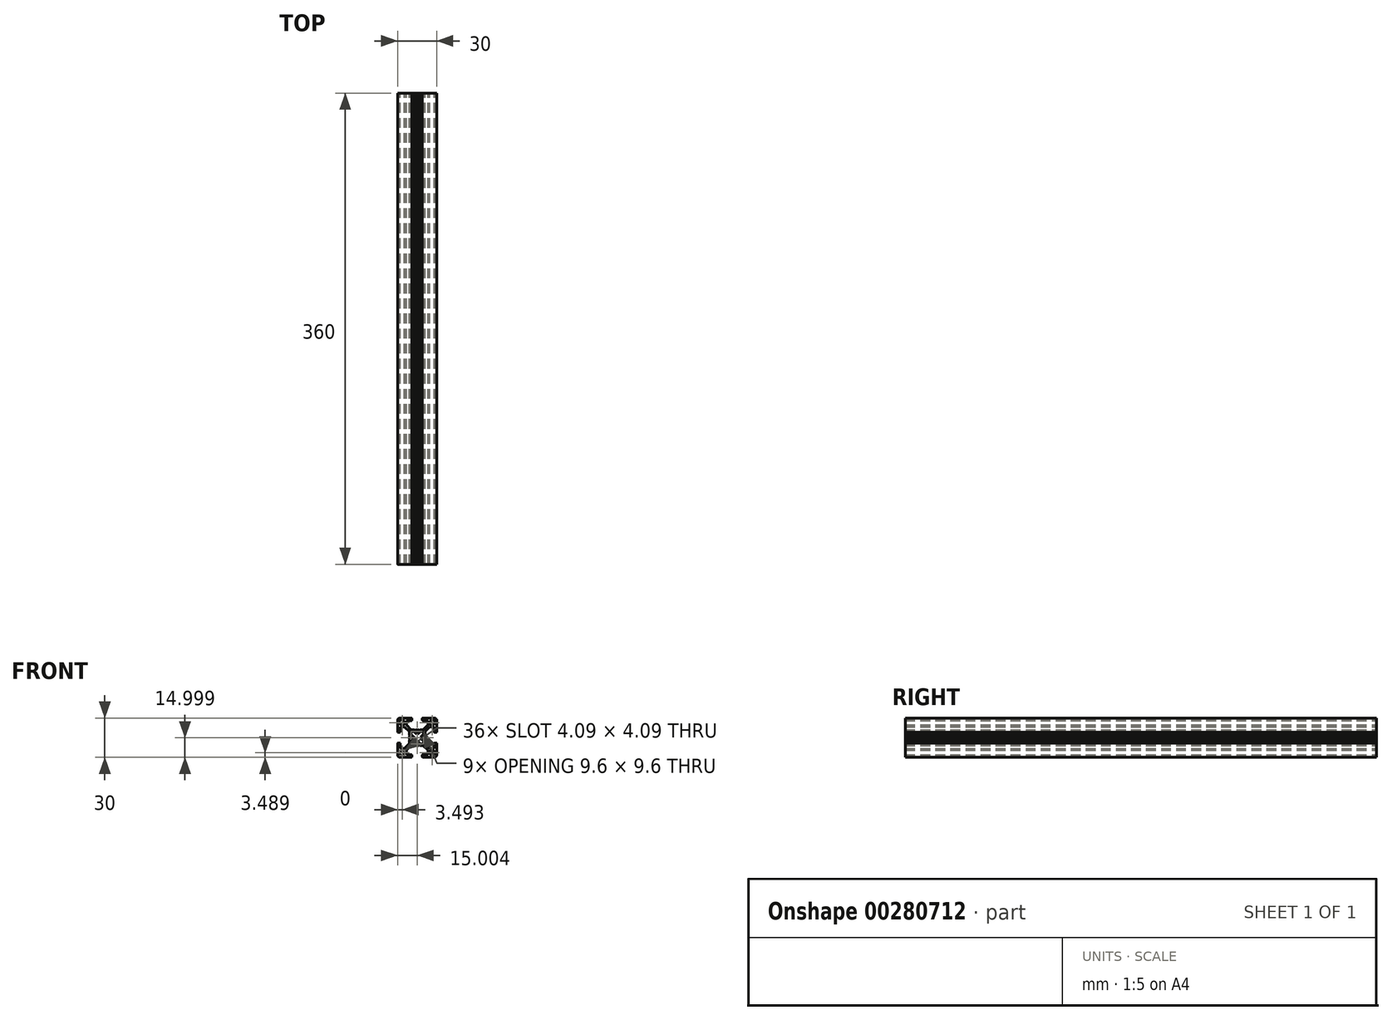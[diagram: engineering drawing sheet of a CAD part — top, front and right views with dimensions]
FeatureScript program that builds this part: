
annotation { "Feature Type Name" : "Feature", "Feature Type Description" : "" }
export const myFeature = defineFeature(function(context is Context, id is Id, definition is map)
    precondition{}
    {
        {
            var Q0;
            Q0=qCreatedBy(makeId("Front.planeOp"),FACE);
            var sketch = newSketch(context, id + "F0", { "sketchPlane" : qUnion([Q0])});
            skArc(sketch, "E0", {"start": v(22.08, 23.36) * mm, "mid": v(21.8, 23.24) * mm, "end": v(21.68, 22.96) * mm});
            skArc(sketch, "E1", {"start": v(21.68, 14.16) * mm, "mid": v(21.8, 13.88) * mm, "end": v(22.08, 13.76) * mm});
            skArc(sketch, "E2", {"start": v(11.48, 5.56) * mm, "mid": v(12.07, 4.15) * mm, "end": v(13.48, 3.56) * mm});
            skLineSegment(sketch, "E3", {"start": v(11.48, 14.16) * mm, "end": v(11.48, 5.56) * mm});
            skLineSegment(sketch, "E4", {"start": v(18.23, 5.56) * mm, "end": v(18.23, 8.9) * mm});
            skLineSegment(sketch, "E5", {"start": v(22.08, 3.56) * mm, "end": v(13.48, 3.56) * mm});
            skLineSegment(sketch, "E6", {"start": v(22.08, 5.56) * mm, "end": v(18.23, 5.56) * mm});
            skLineSegment(sketch, "E7", {"start": v(22.48, 5.16) * mm, "end": v(22.48, 3.96) * mm});
            skLineSegment(sketch, "E8", {"start": v(13.48, 10.3) * mm, "end": v(16.82, 10.3) * mm});
            skLineSegment(sketch, "E9", {"start": v(20.48, 13.97) * mm, "end": v(16.82, 10.3) * mm});
            skLineSegment(sketch, "E10", {"start": v(21.9, 12.56) * mm, "end": v(18.23, 8.9) * mm});
            skLineSegment(sketch, "E11", {"start": v(13.48, 14.16) * mm, "end": v(13.48, 10.3) * mm});
            skLineSegment(sketch, "E12", {"start": v(11.88, 14.56) * mm, "end": v(13.08, 14.56) * mm});
            skArc(sketch, "E13", {"start": v(22.08, 3.56) * mm, "mid": v(22.37, 3.68) * mm, "end": v(22.48, 3.96) * mm});
            skArc(sketch, "E14", {"start": v(22.48, 5.16) * mm, "mid": v(22.37, 5.44) * mm, "end": v(22.08, 5.56) * mm});
            skArc(sketch, "E15", {"start": v(13.48, 14.16) * mm, "mid": v(13.37, 14.44) * mm, "end": v(13.08, 14.56) * mm});
            skArc(sketch, "E16", {"start": v(11.88, 14.56) * mm, "mid": v(11.6, 14.44) * mm, "end": v(11.48, 14.16) * mm});
            skLineSegment(sketch, "E17", {"start": v(20.78, 18.56) * mm, "end": v(20.55, 18.16) * mm});
            skLineSegment(sketch, "E18", {"start": v(20.48, 13.97) * mm, "end": v(20.48, 16.06) * mm});
            skLineSegment(sketch, "E19", {"start": v(20.55, 17.66) * mm, "end": v(20.73, 17.34) * mm});
            skLineSegment(sketch, "E20", {"start": v(20.73, 17.34) * mm, "end": v(20.48, 16.06) * mm});
            skArc(sketch, "E21", {"start": v(20.55, 18.16) * mm, "mid": v(20.48, 17.9) * mm, "end": v(20.55, 17.66) * mm});
            skLineSegment(sketch, "E22", {"start": v(26.08, 12.63) * mm, "end": v(26.48, 12.86) * mm});
            skLineSegment(sketch, "E23", {"start": v(21.9, 12.56) * mm, "end": v(23.98, 12.56) * mm});
            skLineSegment(sketch, "E24", {"start": v(23.98, 12.56) * mm, "end": v(25.26, 12.8) * mm});
            skArc(sketch, "E25", {"start": v(25.58, 12.63) * mm, "mid": v(25.83, 12.56) * mm, "end": v(26.08, 12.63) * mm});
            skLineSegment(sketch, "E26", {"start": v(25.26, 12.8) * mm, "end": v(25.58, 12.63) * mm});
            skArc(sketch, "E27", {"start": v(25.5, 15.3) * mm, "mid": v(26.48, 15.16) * mm, "end": v(27.47, 15.3) * mm});
            skLineSegment(sketch, "E28", {"start": v(21.68, 14.16) * mm, "end": v(21.68, 15.9) * mm});
            skLineSegment(sketch, "E29", {"start": v(22.08, 13.76) * mm, "end": v(23.83, 13.76) * mm});
            skLineSegment(sketch, "E30", {"start": v(24.98, 14.3) * mm, "end": v(24.98, 14.92) * mm});
            skArc(sketch, "E31", {"start": v(25.5, 15.3) * mm, "mid": v(25.15, 15.24) * mm, "end": v(24.98, 14.92) * mm});
            skLineSegment(sketch, "E32", {"start": v(23.9, 13.77) * mm, "end": v(24.66, 13.91) * mm});
            skArc(sketch, "E33", {"start": v(24.66, 13.91) * mm, "mid": v(24.9, 14.05) * mm, "end": v(24.98, 14.3) * mm});
            skArc(sketch, "E34", {"start": v(23.83, 13.76) * mm, "mid": v(23.87, 13.76) * mm, "end": v(23.9, 13.77) * mm});
            skLineSegment(sketch, "E35", {"start": v(22.23, 17.06) * mm, "end": v(22.85, 17.06) * mm});
            skArc(sketch, "E36", {"start": v(22.85, 17.06) * mm, "mid": v(23.17, 17.22) * mm, "end": v(23.23, 17.58) * mm});
            skLineSegment(sketch, "E37", {"start": v(21.7, 15.98) * mm, "end": v(21.84, 16.74) * mm});
            skArc(sketch, "E38", {"start": v(22.23, 17.06) * mm, "mid": v(21.98, 16.97) * mm, "end": v(21.84, 16.74) * mm});
            skArc(sketch, "E39", {"start": v(21.7, 15.98) * mm, "mid": v(21.69, 15.94) * mm, "end": v(21.68, 15.9) * mm});
            skArc(sketch, "E40", {"start": v(30.88, 13.76) * mm, "mid": v(31.17, 13.88) * mm, "end": v(31.28, 14.16) * mm});
            skArc(sketch, "E41", {"start": v(39.48, 3.56) * mm, "mid": v(40.9, 4.15) * mm, "end": v(41.48, 5.56) * mm});
            skLineSegment(sketch, "E42", {"start": v(30.88, 3.56) * mm, "end": v(39.48, 3.56) * mm});
            skLineSegment(sketch, "E43", {"start": v(39.48, 10.3) * mm, "end": v(36.15, 10.3) * mm});
            skLineSegment(sketch, "E44", {"start": v(41.48, 14.16) * mm, "end": v(41.48, 5.56) * mm});
            skLineSegment(sketch, "E45", {"start": v(39.48, 14.16) * mm, "end": v(39.48, 10.3) * mm});
            skLineSegment(sketch, "E46", {"start": v(39.88, 14.56) * mm, "end": v(41.08, 14.56) * mm});
            skLineSegment(sketch, "E47", {"start": v(34.73, 5.56) * mm, "end": v(34.73, 8.9) * mm});
            skLineSegment(sketch, "E48", {"start": v(31.07, 12.56) * mm, "end": v(34.73, 8.9) * mm});
            skLineSegment(sketch, "E49", {"start": v(32.48, 13.97) * mm, "end": v(36.15, 10.3) * mm});
            skLineSegment(sketch, "E50", {"start": v(30.88, 5.56) * mm, "end": v(34.73, 5.56) * mm});
            skLineSegment(sketch, "E51", {"start": v(30.48, 3.96) * mm, "end": v(30.48, 5.16) * mm});
            skArc(sketch, "E52", {"start": v(41.48, 14.16) * mm, "mid": v(41.37, 14.44) * mm, "end": v(41.08, 14.56) * mm});
            skArc(sketch, "E53", {"start": v(39.88, 14.56) * mm, "mid": v(39.6, 14.44) * mm, "end": v(39.48, 14.16) * mm});
            skArc(sketch, "E54", {"start": v(30.88, 5.56) * mm, "mid": v(30.6, 5.44) * mm, "end": v(30.48, 5.16) * mm});
            skArc(sketch, "E55", {"start": v(30.48, 3.96) * mm, "mid": v(30.6, 3.68) * mm, "end": v(30.88, 3.56) * mm});
            skLineSegment(sketch, "E56", {"start": v(26.48, 12.86) * mm, "end": v(26.89, 12.63) * mm});
            skLineSegment(sketch, "E57", {"start": v(31.07, 12.56) * mm, "end": v(28.98, 12.56) * mm});
            skLineSegment(sketch, "E58", {"start": v(27.39, 12.63) * mm, "end": v(27.7, 12.8) * mm});
            skLineSegment(sketch, "E59", {"start": v(27.7, 12.8) * mm, "end": v(28.98, 12.56) * mm});
            skArc(sketch, "E60", {"start": v(26.89, 12.63) * mm, "mid": v(27.14, 12.56) * mm, "end": v(27.39, 12.63) * mm});
            skLineSegment(sketch, "E61", {"start": v(32.42, 18.16) * mm, "end": v(32.18, 18.56) * mm});
            skLineSegment(sketch, "E62", {"start": v(32.48, 13.97) * mm, "end": v(32.48, 16.06) * mm});
            skLineSegment(sketch, "E63", {"start": v(32.48, 16.06) * mm, "end": v(32.23, 17.34) * mm});
            skArc(sketch, "E64", {"start": v(32.42, 17.66) * mm, "mid": v(32.48, 17.9) * mm, "end": v(32.42, 18.16) * mm});
            skLineSegment(sketch, "E65", {"start": v(32.23, 17.34) * mm, "end": v(32.42, 17.66) * mm});
            skArc(sketch, "E66", {"start": v(29.74, 17.58) * mm, "mid": v(29.88, 18.56) * mm, "end": v(29.74, 19.54) * mm});
            skLineSegment(sketch, "E67", {"start": v(30.88, 13.76) * mm, "end": v(29.14, 13.76) * mm});
            skLineSegment(sketch, "E68", {"start": v(31.28, 14.16) * mm, "end": v(31.28, 15.9) * mm});
            skLineSegment(sketch, "E69", {"start": v(30.74, 17.06) * mm, "end": v(30.12, 17.06) * mm});
            skArc(sketch, "E70", {"start": v(29.74, 17.58) * mm, "mid": v(29.8, 17.22) * mm, "end": v(30.12, 17.06) * mm});
            skLineSegment(sketch, "E71", {"start": v(31.28, 15.98) * mm, "end": v(31.13, 16.74) * mm});
            skArc(sketch, "E72", {"start": v(31.13, 16.74) * mm, "mid": v(31, 16.97) * mm, "end": v(30.74, 17.06) * mm});
            skArc(sketch, "E73", {"start": v(31.28, 15.9) * mm, "mid": v(31.28, 15.94) * mm, "end": v(31.28, 15.98) * mm});
            skLineSegment(sketch, "E74", {"start": v(27.98, 14.3) * mm, "end": v(27.98, 14.92) * mm});
            skArc(sketch, "E75", {"start": v(27.98, 14.92) * mm, "mid": v(27.82, 15.24) * mm, "end": v(27.47, 15.3) * mm});
            skLineSegment(sketch, "E76", {"start": v(29.06, 13.77) * mm, "end": v(28.3, 13.91) * mm});
            skArc(sketch, "E77", {"start": v(27.98, 14.3) * mm, "mid": v(28.08, 14.05) * mm, "end": v(28.3, 13.91) * mm});
            skArc(sketch, "E78", {"start": v(29.06, 13.77) * mm, "mid": v(29.1, 13.76) * mm, "end": v(29.14, 13.76) * mm});
            skArc(sketch, "E79", {"start": v(31.28, 22.96) * mm, "mid": v(31.17, 23.24) * mm, "end": v(30.88, 23.36) * mm});
            skArc(sketch, "E80", {"start": v(41.48, 31.56) * mm, "mid": v(40.9, 32.97) * mm, "end": v(39.48, 33.56) * mm});
            skLineSegment(sketch, "E81", {"start": v(41.48, 22.96) * mm, "end": v(41.48, 31.56) * mm});
            skLineSegment(sketch, "E82", {"start": v(34.73, 31.56) * mm, "end": v(34.73, 28.22) * mm});
            skLineSegment(sketch, "E83", {"start": v(30.88, 33.56) * mm, "end": v(39.48, 33.56) * mm});
            skLineSegment(sketch, "E84", {"start": v(30.88, 31.56) * mm, "end": v(34.73, 31.56) * mm});
            skLineSegment(sketch, "E85", {"start": v(30.48, 31.96) * mm, "end": v(30.48, 33.16) * mm});
            skLineSegment(sketch, "E86", {"start": v(39.48, 26.8) * mm, "end": v(36.15, 26.8) * mm});
            skLineSegment(sketch, "E87", {"start": v(32.48, 23.15) * mm, "end": v(36.15, 26.8) * mm});
            skLineSegment(sketch, "E88", {"start": v(31.07, 24.56) * mm, "end": v(34.73, 28.22) * mm});
            skLineSegment(sketch, "E89", {"start": v(39.48, 22.96) * mm, "end": v(39.48, 26.8) * mm});
            skLineSegment(sketch, "E90", {"start": v(41.08, 22.56) * mm, "end": v(39.88, 22.56) * mm});
            skArc(sketch, "E91", {"start": v(30.88, 33.56) * mm, "mid": v(30.6, 33.44) * mm, "end": v(30.48, 33.16) * mm});
            skArc(sketch, "E92", {"start": v(30.48, 31.96) * mm, "mid": v(30.6, 31.68) * mm, "end": v(30.88, 31.56) * mm});
            skArc(sketch, "E93", {"start": v(39.48, 22.96) * mm, "mid": v(39.6, 22.68) * mm, "end": v(39.88, 22.56) * mm});
            skArc(sketch, "E94", {"start": v(41.08, 22.56) * mm, "mid": v(41.37, 22.68) * mm, "end": v(41.48, 22.96) * mm});
            skLineSegment(sketch, "E95", {"start": v(32.18, 18.56) * mm, "end": v(32.42, 18.96) * mm});
            skLineSegment(sketch, "E96", {"start": v(32.48, 23.15) * mm, "end": v(32.48, 21.06) * mm});
            skLineSegment(sketch, "E97", {"start": v(32.42, 19.46) * mm, "end": v(32.23, 19.78) * mm});
            skLineSegment(sketch, "E98", {"start": v(32.23, 19.78) * mm, "end": v(32.48, 21.06) * mm});
            skArc(sketch, "E99", {"start": v(32.42, 18.96) * mm, "mid": v(32.48, 19.21) * mm, "end": v(32.42, 19.46) * mm});
            skLineSegment(sketch, "E100", {"start": v(26.89, 24.5) * mm, "end": v(26.48, 24.26) * mm});
            skLineSegment(sketch, "E101", {"start": v(31.07, 24.56) * mm, "end": v(28.98, 24.56) * mm});
            skLineSegment(sketch, "E102", {"start": v(28.98, 24.56) * mm, "end": v(27.7, 24.31) * mm});
            skArc(sketch, "E103", {"start": v(27.39, 24.5) * mm, "mid": v(27.14, 24.56) * mm, "end": v(26.89, 24.5) * mm});
            skLineSegment(sketch, "E104", {"start": v(27.7, 24.31) * mm, "end": v(27.39, 24.5) * mm});
            skArc(sketch, "E105", {"start": v(27.47, 21.81) * mm, "mid": v(26.48, 21.96) * mm, "end": v(25.5, 21.81) * mm});
            skLineSegment(sketch, "E106", {"start": v(31.28, 22.96) * mm, "end": v(31.28, 21.21) * mm});
            skLineSegment(sketch, "E107", {"start": v(30.88, 23.36) * mm, "end": v(29.14, 23.36) * mm});
            skLineSegment(sketch, "E108", {"start": v(27.98, 22.81) * mm, "end": v(27.98, 22.2) * mm});
            skArc(sketch, "E109", {"start": v(27.47, 21.81) * mm, "mid": v(27.82, 21.88) * mm, "end": v(27.98, 22.2) * mm});
            skLineSegment(sketch, "E110", {"start": v(29.06, 23.35) * mm, "end": v(28.3, 23.2) * mm});
            skArc(sketch, "E111", {"start": v(28.3, 23.2) * mm, "mid": v(28.08, 23.07) * mm, "end": v(27.98, 22.81) * mm});
            skArc(sketch, "E112", {"start": v(29.14, 23.36) * mm, "mid": v(29.1, 23.36) * mm, "end": v(29.06, 23.35) * mm});
            skLineSegment(sketch, "E113", {"start": v(30.74, 20.06) * mm, "end": v(30.12, 20.06) * mm});
            skArc(sketch, "E114", {"start": v(30.12, 20.06) * mm, "mid": v(29.8, 19.9) * mm, "end": v(29.74, 19.54) * mm});
            skLineSegment(sketch, "E115", {"start": v(31.28, 21.14) * mm, "end": v(31.13, 20.38) * mm});
            skArc(sketch, "E116", {"start": v(30.74, 20.06) * mm, "mid": v(31, 20.15) * mm, "end": v(31.13, 20.38) * mm});
            skArc(sketch, "E117", {"start": v(31.28, 21.14) * mm, "mid": v(31.28, 21.18) * mm, "end": v(31.28, 21.21) * mm});
            skArc(sketch, "E118", {"start": v(13.48, 33.56) * mm, "mid": v(12.07, 32.97) * mm, "end": v(11.48, 31.56) * mm});
            skLineSegment(sketch, "E119", {"start": v(22.08, 33.56) * mm, "end": v(13.48, 33.56) * mm});
            skLineSegment(sketch, "E120", {"start": v(13.48, 26.8) * mm, "end": v(16.82, 26.8) * mm});
            skLineSegment(sketch, "E121", {"start": v(11.48, 22.96) * mm, "end": v(11.48, 31.56) * mm});
            skLineSegment(sketch, "E122", {"start": v(13.48, 22.96) * mm, "end": v(13.48, 26.8) * mm});
            skLineSegment(sketch, "E123", {"start": v(13.08, 22.56) * mm, "end": v(11.88, 22.56) * mm});
            skLineSegment(sketch, "E124", {"start": v(18.23, 31.56) * mm, "end": v(18.23, 28.22) * mm});
            skLineSegment(sketch, "E125", {"start": v(21.9, 24.56) * mm, "end": v(18.23, 28.22) * mm});
            skLineSegment(sketch, "E126", {"start": v(20.48, 23.15) * mm, "end": v(16.82, 26.8) * mm});
            skLineSegment(sketch, "E127", {"start": v(22.08, 31.56) * mm, "end": v(18.23, 31.56) * mm});
            skLineSegment(sketch, "E128", {"start": v(22.48, 33.16) * mm, "end": v(22.48, 31.96) * mm});
            skArc(sketch, "E129", {"start": v(11.48, 22.96) * mm, "mid": v(11.6, 22.68) * mm, "end": v(11.88, 22.56) * mm});
            skArc(sketch, "E130", {"start": v(13.08, 22.56) * mm, "mid": v(13.37, 22.68) * mm, "end": v(13.48, 22.96) * mm});
            skArc(sketch, "E131", {"start": v(22.08, 31.56) * mm, "mid": v(22.37, 31.68) * mm, "end": v(22.48, 31.96) * mm});
            skArc(sketch, "E132", {"start": v(22.48, 33.16) * mm, "mid": v(22.37, 33.44) * mm, "end": v(22.08, 33.56) * mm});
            skLineSegment(sketch, "E133", {"start": v(26.48, 24.26) * mm, "end": v(26.08, 24.5) * mm});
            skLineSegment(sketch, "E134", {"start": v(21.9, 24.56) * mm, "end": v(23.98, 24.56) * mm});
            skLineSegment(sketch, "E135", {"start": v(25.58, 24.5) * mm, "end": v(25.26, 24.31) * mm});
            skLineSegment(sketch, "E136", {"start": v(25.26, 24.31) * mm, "end": v(23.98, 24.56) * mm});
            skArc(sketch, "E137", {"start": v(26.08, 24.5) * mm, "mid": v(25.83, 24.56) * mm, "end": v(25.58, 24.5) * mm});
            skLineSegment(sketch, "E138", {"start": v(20.55, 18.96) * mm, "end": v(20.78, 18.56) * mm});
            skLineSegment(sketch, "E139", {"start": v(20.48, 23.15) * mm, "end": v(20.48, 21.06) * mm});
            skLineSegment(sketch, "E140", {"start": v(20.48, 21.06) * mm, "end": v(20.73, 19.78) * mm});
            skArc(sketch, "E141", {"start": v(20.55, 19.46) * mm, "mid": v(20.48, 19.21) * mm, "end": v(20.55, 18.96) * mm});
            skLineSegment(sketch, "E142", {"start": v(20.73, 19.78) * mm, "end": v(20.55, 19.46) * mm});
            skArc(sketch, "E143", {"start": v(23.23, 19.54) * mm, "mid": v(23.08, 18.56) * mm, "end": v(23.23, 17.58) * mm});
            skLineSegment(sketch, "E144", {"start": v(22.08, 23.36) * mm, "end": v(23.83, 23.36) * mm});
            skLineSegment(sketch, "E145", {"start": v(21.68, 22.96) * mm, "end": v(21.68, 21.21) * mm});
            skLineSegment(sketch, "E146", {"start": v(22.23, 20.06) * mm, "end": v(22.85, 20.06) * mm});
            skArc(sketch, "E147", {"start": v(23.23, 19.54) * mm, "mid": v(23.17, 19.9) * mm, "end": v(22.85, 20.06) * mm});
            skLineSegment(sketch, "E148", {"start": v(21.7, 21.14) * mm, "end": v(21.84, 20.38) * mm});
            skArc(sketch, "E149", {"start": v(21.84, 20.38) * mm, "mid": v(21.98, 20.15) * mm, "end": v(22.23, 20.06) * mm});
            skArc(sketch, "E150", {"start": v(21.68, 21.21) * mm, "mid": v(21.69, 21.18) * mm, "end": v(21.7, 21.14) * mm});
            skLineSegment(sketch, "E151", {"start": v(24.98, 22.81) * mm, "end": v(24.98, 22.2) * mm});
            skArc(sketch, "E152", {"start": v(24.98, 22.2) * mm, "mid": v(25.15, 21.88) * mm, "end": v(25.5, 21.81) * mm});
            skLineSegment(sketch, "E153", {"start": v(23.9, 23.35) * mm, "end": v(24.66, 23.2) * mm});
            skArc(sketch, "E154", {"start": v(24.98, 22.81) * mm, "mid": v(24.9, 23.07) * mm, "end": v(24.66, 23.2) * mm});
            skArc(sketch, "E155", {"start": v(23.9, 23.35) * mm, "mid": v(23.87, 23.36) * mm, "end": v(23.83, 23.36) * mm});
            skArc(sketch, "E156", {"start": v(14.13, 8.64) * mm, "mid": v(13.44, 5.52) * mm, "end": v(16.57, 6.2) * mm});
            skLineSegment(sketch, "E157", {"start": v(16.94, 7.22) * mm, "end": v(16.57, 6.2) * mm});
            skLineSegment(sketch, "E158", {"start": v(15.14, 9.01) * mm, "end": v(14.13, 8.64) * mm});
            skArc(sketch, "E159", {"start": v(16.94, 7.22) * mm, "mid": v(16.61, 8.69) * mm, "end": v(15.14, 9.01) * mm});
            skArc(sketch, "E160", {"start": v(16.57, 30.9) * mm, "mid": v(13.44, 31.6) * mm, "end": v(14.13, 28.47) * mm});
            skLineSegment(sketch, "E161", {"start": v(16.94, 29.9) * mm, "end": v(16.57, 30.9) * mm});
            skLineSegment(sketch, "E162", {"start": v(15.14, 28.1) * mm, "end": v(14.13, 28.47) * mm});
            skArc(sketch, "E163", {"start": v(15.14, 28.1) * mm, "mid": v(16.61, 28.43) * mm, "end": v(16.94, 29.9) * mm});
            skArc(sketch, "E164", {"start": v(36.4, 6.2) * mm, "mid": v(39.53, 5.52) * mm, "end": v(38.83, 8.64) * mm});
            skLineSegment(sketch, "E165", {"start": v(36.03, 7.22) * mm, "end": v(36.4, 6.2) * mm});
            skLineSegment(sketch, "E166", {"start": v(37.83, 9.01) * mm, "end": v(38.83, 8.64) * mm});
            skArc(sketch, "E167", {"start": v(37.83, 9.01) * mm, "mid": v(36.36, 8.69) * mm, "end": v(36.03, 7.22) * mm});
            skArc(sketch, "E168", {"start": v(38.83, 28.47) * mm, "mid": v(39.53, 31.6) * mm, "end": v(36.4, 30.9) * mm});
            skLineSegment(sketch, "E169", {"start": v(36.03, 29.9) * mm, "end": v(36.4, 30.9) * mm});
            skLineSegment(sketch, "E170", {"start": v(37.83, 28.1) * mm, "end": v(38.83, 28.47) * mm});
            skArc(sketch, "E171", {"start": v(36.03, 29.9) * mm, "mid": v(36.36, 28.43) * mm, "end": v(37.83, 28.1) * mm});
            skLineSegment(sketch, "E172", {"start": v(26.48, 0.56) * mm, "end": v(26.48, 36.56) * mm});
            skLineSegment(sketch, "E173", {"start": v(44.48, 18.56) * mm, "end": v(8.48, 18.56) * mm});
            skSolve(sketch);
        }
        {
            var Q0;
            Q0 = qSketchRegion(id + "F0", true);
            extrude(context, id + "F1", {"entities" : qUnion([Q0]), "depth" : 360 * mm});
        }
    });
